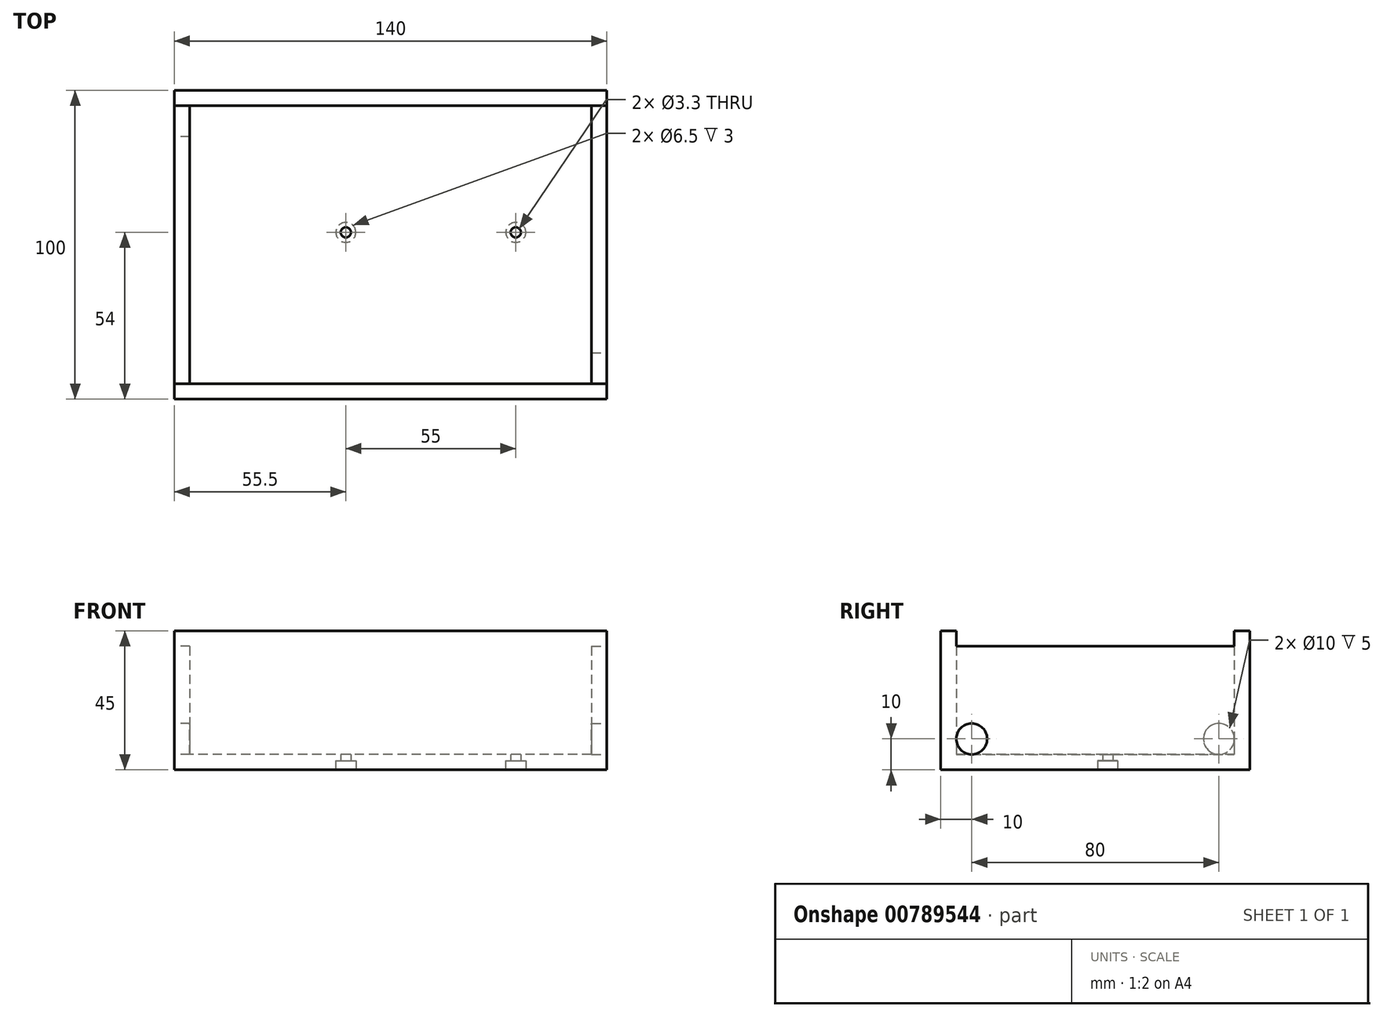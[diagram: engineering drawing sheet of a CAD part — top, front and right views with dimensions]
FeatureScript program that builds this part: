
annotation { "Feature Type Name" : "Feature", "Feature Type Description" : "" }
export const myFeature = defineFeature(function(context is Context, id is Id, definition is map)
    precondition{}
    {
        {
            var Q0;
            Q0=qCreatedBy(makeId("Top.planeOp"),FACE);
            var sketch = newSketch(context, id + "F0", { "sketchPlane" : qUnion([Q0])});
            skLineSegment(sketch, "E0.bottom", {"start": v(-70, 50) * mm, "end": v(70, 50) * mm});
            skLineSegment(sketch, "E0.top", {"start": v(-70, -50) * mm, "end": v(70, -50) * mm});
            skLineSegment(sketch, "E0.left", {"start": v(-70, 50) * mm, "end": v(-70, -50) * mm});
            skLineSegment(sketch, "E0.right", {"start": v(70, 50) * mm, "end": v(70, -50) * mm});
            skSolve(sketch);
        }
        {
            var Q0;
            Q0=makeQuery(id+"F0.imprint","IMPRINT",FACE,{"disambiguationData":[TD([[makeQuery(id+"F0.imprint","IMPRINT",EDGE,{"derivedFrom":sQuery(id+"F0.wireOp",EDGE,"E0.bottom")}),-1.0]])]});
            extrude(context, id + "F1", {"entities" : qUnion([Q0]), "depth" : 5 * mm, "offsetDistance" : 25 * mm});
        }
        {
            var Q0;
            Q0=makeQuery(id+"F1.opExtrude","CAP_FACE",FACE,{"disambiguationData":[OSD([sQuery(id+"F0.wireOp",EDGE,"E0.bottom"),sQuery(id+"F0.wireOp",EDGE,"E0.top"),sQuery(id+"F0.wireOp",EDGE,"E0.left"),sQuery(id+"F0.wireOp",EDGE,"E0.right")])],"isStart":false});
            var sketch = newSketch(context, id + "F2", { "sketchPlane" : qUnion([Q0])});
            skLineSegment(sketch, "E1.0", {"start": v(-65, 45) * mm, "end": v(-65, -45) * mm});
            skLineSegment(sketch, "E1.1", {"start": v(65, 45) * mm, "end": v(-65, 45) * mm});
            skLineSegment(sketch, "E1.2", {"start": v(65, -45) * mm, "end": v(65, 45) * mm});
            skLineSegment(sketch, "E1.3", {"start": v(-65, -45) * mm, "end": v(65, -45) * mm});
            skLineSegment(sketch, "E2.bottom", {"start": v(-70, 50) * mm, "end": v(70, 50) * mm});
            skLineSegment(sketch, "E2.top", {"start": v(-70, -50) * mm, "end": v(70, -50) * mm});
            skLineSegment(sketch, "E2.left", {"start": v(-70, 50) * mm, "end": v(-70, -50) * mm});
            skLineSegment(sketch, "E2.right", {"start": v(70, 50) * mm, "end": v(70, -50) * mm});
            skSolve(sketch);
        }
        {
            var Q0;
            Q0=makeQuery(id+"F2.imprint","IMPRINT",FACE,{"disambiguationData":[TD([[makeQuery(id+"F2.imprint","IMPRINT",EDGE,{"derivedFrom":sQuery(id+"F2.wireOp",EDGE,"E1.0")}),-1.0]])]});
            extrude(context, id + "F3", {"entities" : qUnion([Q0]), "operationType" : NewBodyOperationType.ADD, "depth" : 40 * mm, "offsetDistance" : 25 * mm});
        }
        {
            var Q0;
            Q0=makeQuery(id+"F1.opExtrude","CAP_FACE",FACE,{"disambiguationData":[OSD([sQuery(id+"F0.wireOp",EDGE,"E0.bottom"),sQuery(id+"F0.wireOp",EDGE,"E0.top"),sQuery(id+"F0.wireOp",EDGE,"E0.left"),sQuery(id+"F0.wireOp",EDGE,"E0.right")])],"isStart":true});
            var sketch = newSketch(context, id + "F4", { "sketchPlane" : qUnion([Q0])});
            skPoint(sketch, "E3", {"position": v(40.5, -4) * mm});
            skPoint(sketch, "E4", {"position": v(-14.5, -4) * mm});
            skLineSegment(sketch, "E5.0", {"start": v(-65, -45) * mm, "end": v(-65, 45) * mm, "construction": true});
            skLineSegment(sketch, "E6.0.0", {"start": v(-65, -45) * mm, "end": v(65, -45) * mm, "construction": true});
            skSolve(sketch);
        }
        {
            var Q0;
            Q0=sQuery(id+"F4.wireOp",VERTEX,"E3");
            var Q1;
            Q1=sQuery(id+"F4.wireOp",VERTEX,"E4");
            var Q2;
            Q2=makeQuery(id+"F1.opExtrude","SWEPT_BODY",BODY,{"disambiguationData":[OSD([sQuery(id+"F0.wireOp",EDGE,"E0.bottom"),sQuery(id+"F0.wireOp",EDGE,"E0.top"),sQuery(id+"F0.wireOp",EDGE,"E0.left"),sQuery(id+"F0.wireOp",EDGE,"E0.right")])]});
            hole(context, id + "F5", {"style" : HoleStyle.C_BORE, "endStyle" : HoleEndStyle.THROUGH, "standardTappedOrClearance" : lookupTablePath({ "standard" : "ISO", "fit" : "Normal", "size" : "M3", "type" : "Clearance" }), "standardBlindInLast" : lookupTablePath({ "fit" : "Standard", "standard" : "ISO", "size" : "M3", "type" : "Clearance" }), "holeDiameter" : 3.3 * mm, "cBoreDiameter" : 6.5 * mm, "cBoreDepth" : 3 * mm, "majorDiameter" : 5 * mm, "isTappedThrough" : true, "tappedDepth" : 12 * mm, "tapClearance" : 3, "locations" : qUnion([Q0, Q1]), "scope" : qUnion([Q2])});
        }
        {
            var Q0;
            Q0=makeQuery(id+"F3.boolean.opBoolean","MERGE",FACE,{"derivedFrom":[makeQuery(id+"F1.opExtrude","SWEPT_FACE",FACE,{"disambiguationData":[OSD([sQuery(id+"F0.wireOp",EDGE,"E0.right")])]}),makeQuery(id+"F3.opExtrude","SWEPT_FACE",FACE,{"disambiguationData":[OSD([sQuery(id+"F2.wireOp",EDGE,"E2.right")])]})]});
            var sketch = newSketch(context, id + "F6", { "sketchPlane" : qUnion([Q0])});
            skPoint(sketch, "E7", {"position": v(-40, 10) * mm});
            skSolve(sketch);
        }
        {
            var Q0;
            Q0=sQuery(id+"F6.wireOp",VERTEX,"E7");
            var Q1;
            Q1=makeQuery(id+"F1.opExtrude","SWEPT_BODY",BODY,{"disambiguationData":[OSD([sQuery(id+"F0.wireOp",EDGE,"E0.bottom"),sQuery(id+"F0.wireOp",EDGE,"E0.top"),sQuery(id+"F0.wireOp",EDGE,"E0.left"),sQuery(id+"F0.wireOp",EDGE,"E0.right")])]});
            hole(context, id + "F7", {"style" : HoleStyle.SIMPLE, "endStyle" : HoleEndStyle.BLIND, "standardTappedOrClearance" : lookupTablePath({ "standard" : "ISO", "size" : "10", "type" : "Drilled" }), "standardBlindInLast" : lookupTablePath({ "standard" : "ISO", "size" : "10", "type" : "Drilled" }), "holeDiameter" : 10 * mm, "majorDiameter" : 5 * mm, "holeDepth" : 12 * mm, "isTappedThrough" : true, "tappedDepth" : 12 * mm, "tapClearance" : 3, "locations" : qUnion([Q0]), "scope" : qUnion([Q1])});
        }
        {
            var Q0;
            Q0=makeQuery(id+"F3.boolean.opBoolean","MERGE",FACE,{"derivedFrom":[makeQuery(id+"F1.opExtrude","SWEPT_FACE",FACE,{"disambiguationData":[OSD([sQuery(id+"F0.wireOp",EDGE,"E0.left")])]}),makeQuery(id+"F3.opExtrude","SWEPT_FACE",FACE,{"disambiguationData":[OSD([sQuery(id+"F2.wireOp",EDGE,"E2.left")])]})]});
            var sketch = newSketch(context, id + "F8", { "sketchPlane" : qUnion([Q0])});
            skPoint(sketch, "E8", {"position": v(-40, 10) * mm});
            skSolve(sketch);
        }
        {
            var Q0;
            Q0=sQuery(id+"F8.wireOp",VERTEX,"E8");
            var Q1;
            Q1=makeQuery(id+"F1.opExtrude","SWEPT_BODY",BODY,{"disambiguationData":[OSD([sQuery(id+"F0.wireOp",EDGE,"E0.bottom"),sQuery(id+"F0.wireOp",EDGE,"E0.top"),sQuery(id+"F0.wireOp",EDGE,"E0.left"),sQuery(id+"F0.wireOp",EDGE,"E0.right")])]});
            hole(context, id + "F9", {"style" : HoleStyle.SIMPLE, "endStyle" : HoleEndStyle.BLIND, "standardTappedOrClearance" : lookupTablePath({ "standard" : "ISO", "size" : "10", "type" : "Drilled" }), "standardBlindInLast" : lookupTablePath({ "standard" : "ISO", "size" : "10", "type" : "Drilled" }), "holeDiameter" : 10 * mm, "majorDiameter" : 5 * mm, "holeDepth" : 12 * mm, "isTappedThrough" : true, "tappedDepth" : 12 * mm, "tapClearance" : 3, "locations" : qUnion([Q0]), "scope" : qUnion([Q1])});
        }
        {
            var Q0;
            Q0=makeQuery(id+"F3.opExtrude","CAP_FACE",FACE,{"disambiguationData":[OSD([sQuery(id+"F2.wireOp",EDGE,"E1.0"),sQuery(id+"F2.wireOp",EDGE,"E1.1"),sQuery(id+"F2.wireOp",EDGE,"E1.2"),sQuery(id+"F2.wireOp",EDGE,"E1.3"),sQuery(id+"F2.wireOp",EDGE,"E2.bottom"),sQuery(id+"F2.wireOp",EDGE,"E2.top"),sQuery(id+"F2.wireOp",EDGE,"E2.left"),sQuery(id+"F2.wireOp",EDGE,"E2.right")])],"isStart":false});
            var sketch = newSketch(context, id + "F10", { "sketchPlane" : qUnion([Q0])});
            skLineSegment(sketch, "E9.bottom", {"start": v(65, 45) * mm, "end": v(70, 45) * mm});
            skLineSegment(sketch, "E9.top", {"start": v(65, -45) * mm, "end": v(70, -45) * mm});
            skLineSegment(sketch, "E9.left", {"start": v(65, 45) * mm, "end": v(65, -45) * mm});
            skLineSegment(sketch, "E9.right", {"start": v(70, 45) * mm, "end": v(70, -45) * mm});
            skLineSegment(sketch, "E10.bottom", {"start": v(-65, 45) * mm, "end": v(-70, 45) * mm});
            skLineSegment(sketch, "E10.top", {"start": v(-65, -45) * mm, "end": v(-70, -45) * mm});
            skLineSegment(sketch, "E10.left", {"start": v(-65, 45) * mm, "end": v(-65, -45) * mm});
            skLineSegment(sketch, "E10.right", {"start": v(-70, 45) * mm, "end": v(-70, -45) * mm});
            skSolve(sketch);
        }
        {
            var Q0;
            Q0=makeQuery(id+"F10.imprint","IMPRINT",FACE,{"disambiguationData":[TD([[makeQuery(id+"F10.imprint","IMPRINT",EDGE,{"derivedFrom":sQuery(id+"F10.wireOp",EDGE,"E10.bottom")}),1.0]])]});
            var Q1;
            Q1=makeQuery(id+"F10.imprint","IMPRINT",FACE,{"disambiguationData":[TD([[makeQuery(id+"F10.imprint","IMPRINT",EDGE,{"derivedFrom":sQuery(id+"F10.wireOp",EDGE,"E9.bottom")}),-1.0]])]});
            extrude(context, id + "F11", {"entities" : qUnion([Q0, Q1]), "operationType" : NewBodyOperationType.REMOVE, "oppositeDirection" : true, "depth" : 5 * mm, "offsetDistance" : 25 * mm});
        }
    });
